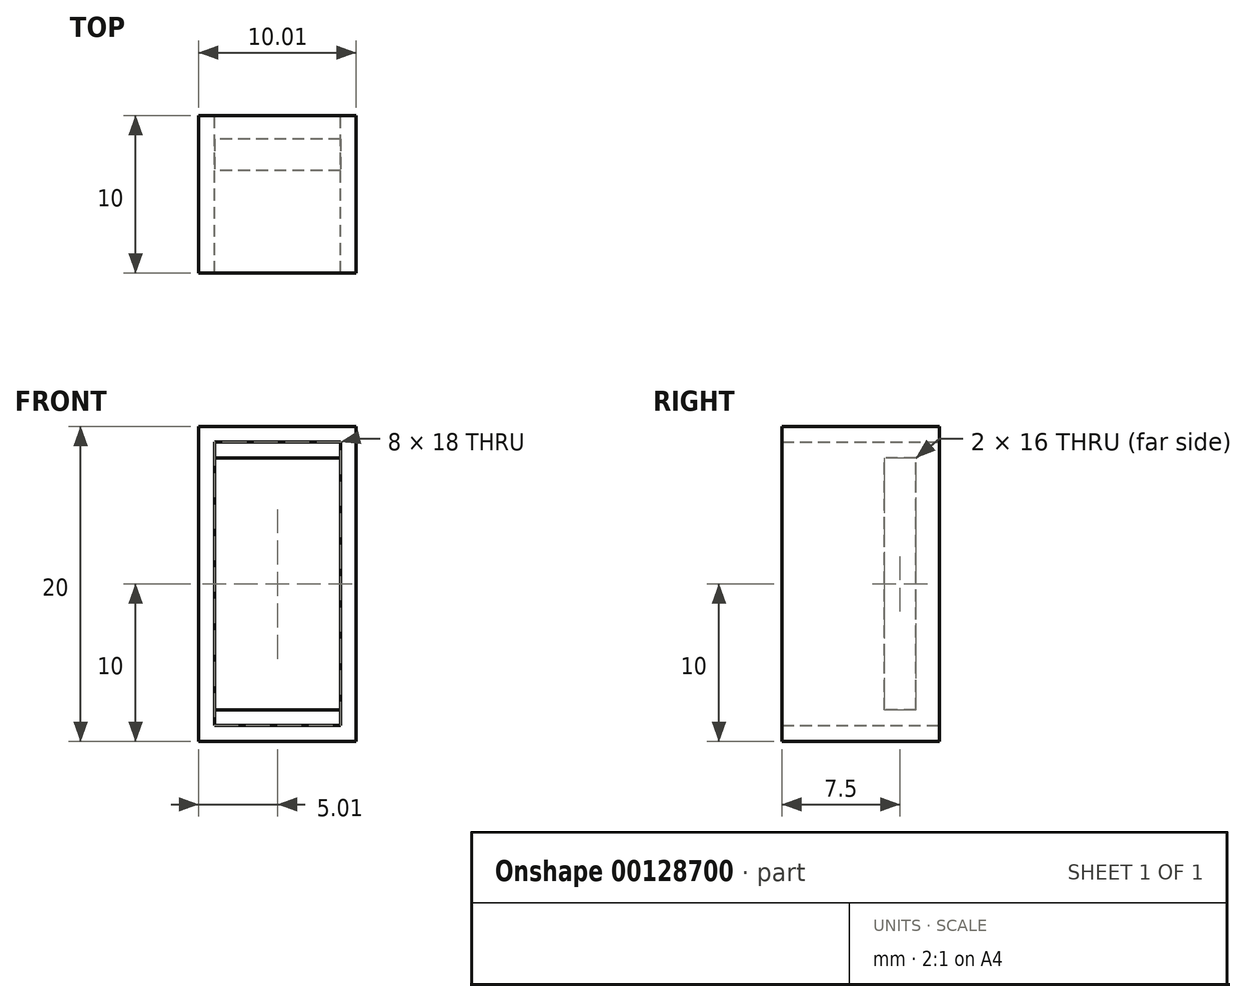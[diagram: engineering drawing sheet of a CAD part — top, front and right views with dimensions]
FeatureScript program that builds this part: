
annotation { "Feature Type Name" : "Feature", "Feature Type Description" : "" }
export const myFeature = defineFeature(function(context is Context, id is Id, definition is map)
    precondition{}
    {
        {
            var Q0;
            Q0=qCreatedBy(makeId("Front.planeOp"),FACE);
            var sketch = newSketch(context, id + "F0", { "sketchPlane" : qUnion([Q0])});
            skLineSegment(sketch, "E0.bottom", {"start": v(-1, 19) * mm, "end": v(9, 19) * mm});
            skLineSegment(sketch, "E0.top", {"start": v(-1, -1) * mm, "end": v(9, -1) * mm});
            skLineSegment(sketch, "E0.left", {"start": v(-1, 19) * mm, "end": v(-1, -1) * mm});
            skLineSegment(sketch, "E0.right", {"start": v(9, 19) * mm, "end": v(9, -1) * mm});
            skLineSegment(sketch, "E1.bottom", {"start": v(0, 18) * mm, "end": v(8, 18) * mm});
            skLineSegment(sketch, "E1.top", {"start": v(0, 0) * mm, "end": v(8, 0) * mm});
            skLineSegment(sketch, "E1.left", {"start": v(0, 18) * mm, "end": v(0, 0) * mm});
            skLineSegment(sketch, "E1.right", {"start": v(8, 18) * mm, "end": v(8, 0) * mm});
            skSolve(sketch);
        }
        {
            var Q0;
            Q0 = qSketchRegion(id + "F0", true);
            extrude(context, id + "F1", {"entities" : qUnion([Q0]), "depth" : 10 * mm});
        }
        {
            var Q0;
            Q0=makeQuery(id+"F1.opExtrude","SWEPT_FACE",FACE,{"disambiguationData":[OSD([sQuery(id+"F0.wireOp",EDGE,"E0.left")])]});
            var sketch = newSketch(context, id + "F2", { "sketchPlane" : qUnion([Q0])});
            skLineSegment(sketch, "E2.bottom", {"start": v(3.5, 17) * mm, "end": v(1.5, 17) * mm});
            skLineSegment(sketch, "E2.top", {"start": v(3.5, 1) * mm, "end": v(1.5, 1) * mm});
            skLineSegment(sketch, "E2.left", {"start": v(3.5, 17) * mm, "end": v(3.5, 1) * mm});
            skLineSegment(sketch, "E2.right", {"start": v(1.5, 17) * mm, "end": v(1.5, 1) * mm});
            skSolve(sketch);
        }
        {
            var Q0;
            Q0 = qSketchRegion(id + "F2", true);
            extrude(context, id + "F3", {"entities" : qUnion([Q0]), "operationType" : NewBodyOperationType.ADD, "oppositeDirection" : true, "depth" : 10 * mm, "hasSecondDirection" : true, "secondDirectionOppositeDirection" : false, "secondDirectionDepth" : 0.01 * mm});
        }
    });
